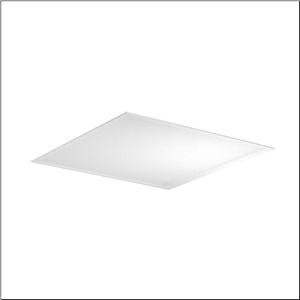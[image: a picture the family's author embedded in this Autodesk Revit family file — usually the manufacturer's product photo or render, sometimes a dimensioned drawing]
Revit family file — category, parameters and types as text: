
# Revit family: apollon_r__31_square_51mp12wd2342_f4b0
name_source: partatom
category: Lighting Fixtures
units: mm (PartAtom-declared; Revit-internal decimal feet)

## family parameters
Cut with Voids When Loaded = No
Host = Face
Light Source = No
Part Type = Normal
Room Calculation Point = No
Round Connector Dimension = Use Diameter
Shared = No

## types (1)
- Apollon® 31 square (1 x LED, 3600 lm, 27.5 W, 3000K)
    Apparent Load = 28 VA
    CIE Flux Codes = 61 87 97 100 100
    Color Rendering = 80
    Color Temperature = 3000K
    Default Elevation = 1800 mm
    Description = Apollon® 31 square, office luminaire, primary optical cover: micro prismatic cover, of PMMA, CAT 2 (L<= 3000cd/m²), light emission: direct distribution, primary light characteristic: symmetric, installation type: lay-in mounting, LED, rated luminous flux: 3.600lm, luminous efficacy: 130lm/W, light colour: 830, colour temperature: 3000K, with terminal, 5-pole, mains connection: 220..240V, AC/DC, 0/50..60Hz, rated input power: 27.5W, housing, of aluminium, traffic white (RAL 9016), module: M600, length: 595mm, width: 595mm, height: 32mm, housing upper side, of sheet steel, galvanised, protection rating (complete): IP20, protection rating (on room side): IP40, insulation class (complete): insulation class II (safety insulation), certification: CE, ENEC, impact resistance: IK03, permissible operating ambient temperature: -20..+40°C, permissible storage temperature: -20..+60°C, packaging unit: 1 piece
    Height = 0 mm  [stored 0 ft]
    Lamp = 1 x LED
    Lamp Light Flux = 3600 lm
    Lamp Power = 27.5 W
    Lamp count = 1
    Length = 595 mm
    Luminous efficacy = 131 lm/W
    Manufacturer = Siteco
    ModVariant = No
    Model = 51MP12WD2342
    Mounting Place = Ceiling
    Mounting Type = Recessed
    Number of Poles = 1
    OnlyDefault = Yes
    Power Factor = 1
    Product Name = Apollon® 31 square
    Product group = office luminaire | ceiling recessed
    ProductGroupID = 400
    Protection Class = Protection class II
    Protection Degree = IP 20
    RLX_Detail_Level = 1
    RLX_Emergency_Light_Flux = 0 lm
    RLX_Emergency_Type = 0
    RLX_Emergency_Type_DB = No
    RlxData = <blob elided: 12493 chars, md5=1976a931>
    Socket = socket
    Standby Power = 0 W
    System Light Flux = 3600 lm
    System Power = 28 W
    Type Comments = Product without accessories
    Type Image = l_1291035.jpg
    URL = http://relux.com
    VarID = ---
    Voltage = 0 V
    Weight = 0.00 kg
    Width = 595 mm

note: [stored X ft] marks values corroborated as IEEE doubles in the binary element streams (Revit-internal decimal feet)

## geometry (parser evidence)
native form markers: Sweep x9
no freeform markers — native parametric forms only
